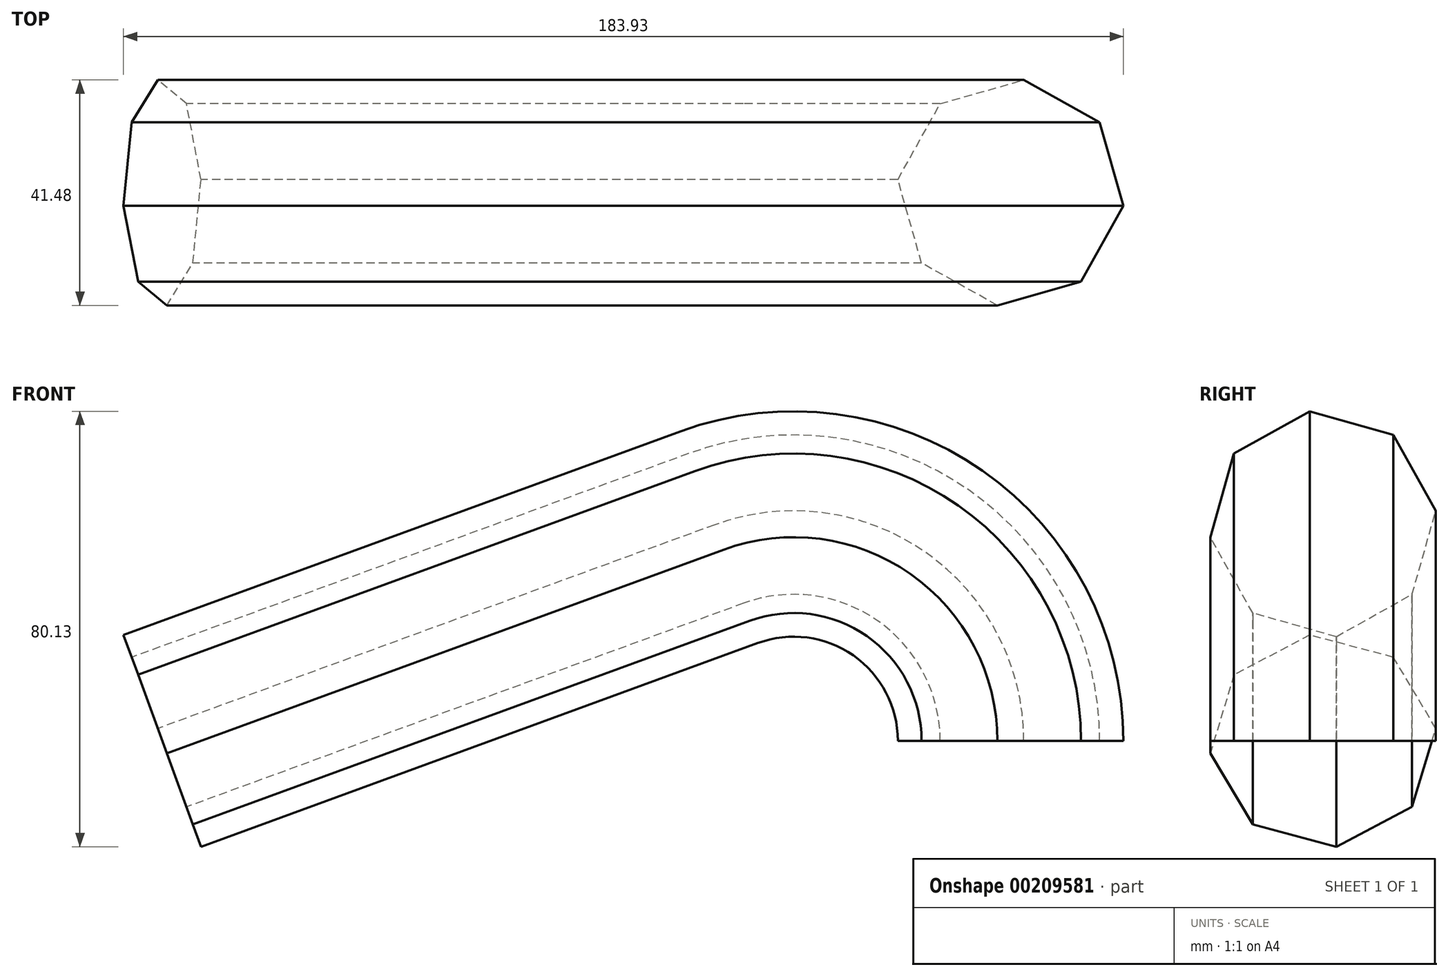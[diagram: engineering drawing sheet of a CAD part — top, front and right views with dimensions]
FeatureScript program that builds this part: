
annotation { "Feature Type Name" : "Feature", "Feature Type Description" : "" }
export const myFeature = defineFeature(function(context is Context, id is Id, definition is map)
    precondition{}
    {
        {
            var Q0;
            Q0=qCreatedBy(makeId("Top.planeOp"),FACE);
            var sketch = newSketch(context, id + "F0", { "sketchPlane" : qUnion([Q0])});
            skCircle(sketch, "E0.cCircle", {"center": v(0, 0) * mm, "radius": 19.3 * mm, "construction": true});
            skLineSegment(sketch, "E0.0", {"start": v(-20.74, 2.43) * mm, "end": v(-12.95, 16.38) * mm});
            skLineSegment(sketch, "E0.1", {"start": v(-12.95, 16.38) * mm, "end": v(2.43, 20.74) * mm});
            skLineSegment(sketch, "E0.2", {"start": v(2.43, 20.74) * mm, "end": v(16.38, 12.95) * mm});
            skLineSegment(sketch, "E0.3", {"start": v(16.38, 12.95) * mm, "end": v(20.74, -2.43) * mm});
            skLineSegment(sketch, "E0.4", {"start": v(20.74, -2.43) * mm, "end": v(12.95, -16.38) * mm});
            skLineSegment(sketch, "E0.5", {"start": v(12.95, -16.38) * mm, "end": v(-2.43, -20.74) * mm});
            skLineSegment(sketch, "E0.6", {"start": v(-2.43, -20.74) * mm, "end": v(-16.38, -12.95) * mm});
            skLineSegment(sketch, "E0.7", {"start": v(-16.38, -12.95) * mm, "end": v(-20.74, 2.43) * mm});
            skPoint(sketch, "E0.0.midPoint", {"position": v(-16.84, 9.4) * mm});
            skSolve(sketch);
        }
        {
            var Q0;
            Q0=qCreatedBy(makeId("Front.planeOp"),FACE);
            var sketch = newSketch(context, id + "F1", { "sketchPlane" : qUnion([Q0])});
            skArc(sketch, "E1", {"start": v(0, 0) * mm, "mid": v(-17.05, 32.71) * mm, "end": v(-53.62, 37.48) * mm});
            skLineSegment(sketch, "E2", {"start": v(0, 0) * mm, "end": v(-124.93, 0) * mm, "construction": true});
            skLineSegment(sketch, "E3", {"start": v(-53.62, 37.48) * mm, "end": v(-156.06, 0) * mm});
            skSolve(sketch);
        }
        {
            var Q0;
            Q0 = qSketchRegion(id + "F0", true);
            var Q1;
            Q1=sQuery(id+"F1.wireOp",EDGE,"E1");
            var Q2;
            Q2=sQuery(id+"F1.wireOp",EDGE,"E3");
            sweep(context, id + "F2", {"profiles" : qUnion([Q0]), "path" : qUnion([Q1, Q2])});
        }
    });
